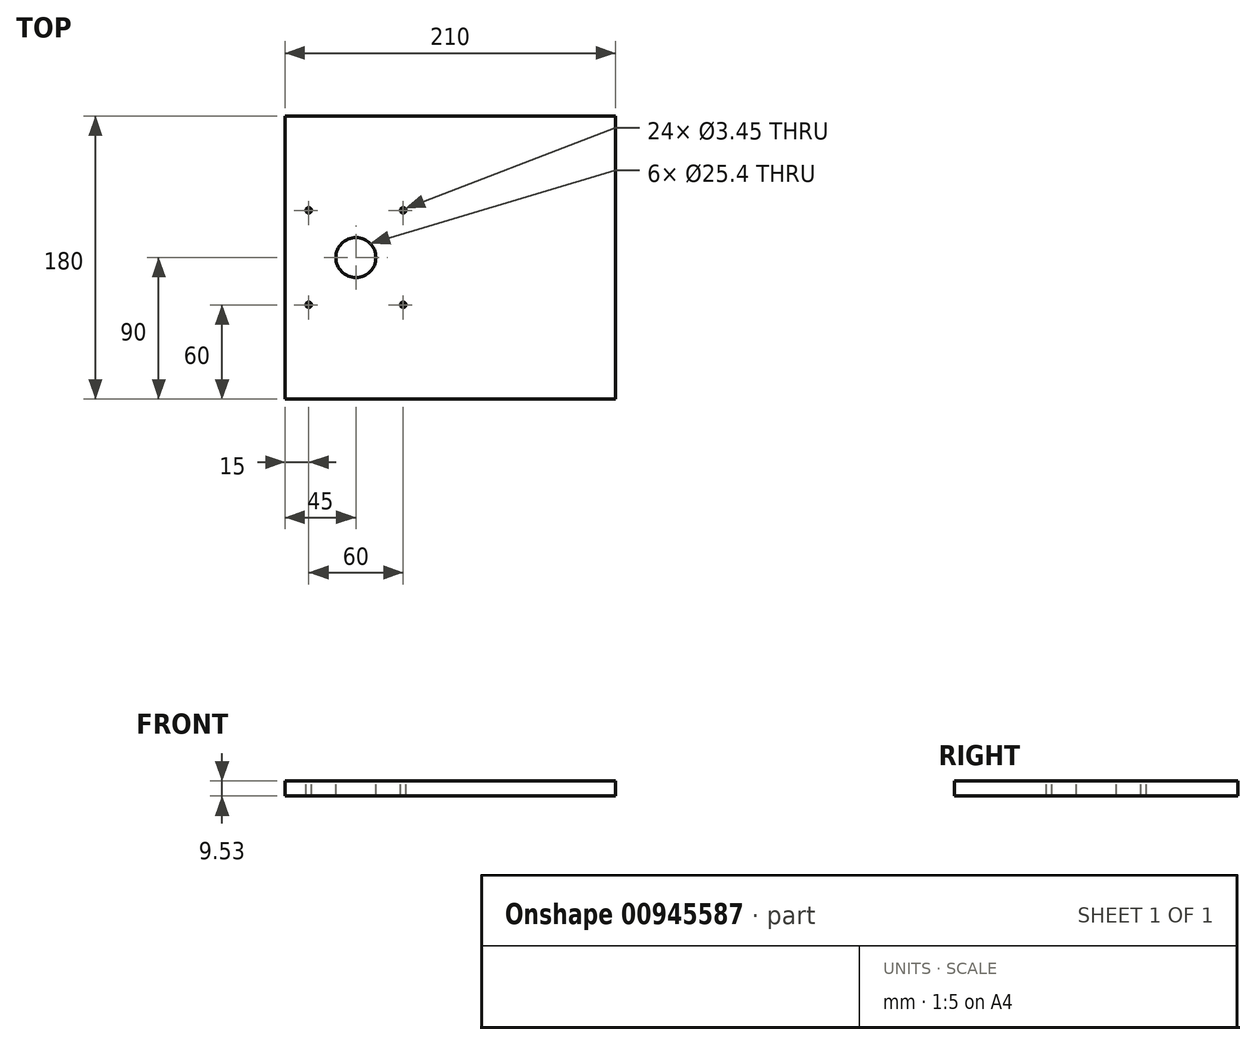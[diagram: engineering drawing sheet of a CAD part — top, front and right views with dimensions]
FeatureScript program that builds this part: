
annotation { "Feature Type Name" : "Feature", "Feature Type Description" : "" }
export const myFeature = defineFeature(function(context is Context, id is Id, definition is map)
    precondition{}
    {
        {
            var Q0;
            Q0=qCreatedBy(makeId("Top.planeOp"),FACE);
            var sketch = newSketch(context, id + "F0", { "sketchPlane" : qUnion([Q0])});
            skLineSegment(sketch, "E0.bottom", {"start": v(105, 90) * mm, "end": v(-105, 90) * mm});
            skLineSegment(sketch, "E0.top", {"start": v(105, -90) * mm, "end": v(-105, -90) * mm});
            skLineSegment(sketch, "E0.left", {"start": v(105, 90) * mm, "end": v(105, -90) * mm});
            skLineSegment(sketch, "E0.right", {"start": v(-105, 90) * mm, "end": v(-105, -90) * mm});
            skPoint(sketch, "E0.middle", {"position": v(0, 0) * mm});
            skSolve(sketch);
        }
        {
            var Q0;
            Q0=qSketchRegion(id+"F0",true);
            extrude(context, id + "F1", {"entities" : qUnion([Q0]), "depth" : 9.52 * mm, "offsetDistance" : 25 * mm});
        }
        {
            var Q0;
            Q0=makeQuery(id+"F1.opExtrude","CAP_FACE",FACE,{"disambiguationData":[OSD([sQuery(id+"F0.wireOp",EDGE,"E0.bottom"),sQuery(id+"F0.wireOp",EDGE,"E0.top"),sQuery(id+"F0.wireOp",EDGE,"E0.left"),sQuery(id+"F0.wireOp",EDGE,"E0.right")])],"isStart":false});
            var sketch = newSketch(context, id + "F2", { "sketchPlane" : qUnion([Q0])});
            skCircle(sketch, "E1", {"center": v(-60, 0) * mm, "radius": 12.7 * mm});
            skCircle(sketch, "E2", {"center": v(-30, 30) * mm, "radius": 1.73 * mm});
            skCircle(sketch, "E3", {"center": v(-30, -30) * mm, "radius": 1.73 * mm});
            skCircle(sketch, "E4", {"center": v(-90, -30) * mm, "radius": 1.73 * mm});
            skCircle(sketch, "E5", {"center": v(-90, 30) * mm, "radius": 1.73 * mm});
            skLineSegment(sketch, "E6", {"start": v(-30, 30) * mm, "end": v(-90, -30) * mm, "construction": true});
            skLineSegment(sketch, "E7", {"start": v(-90, 30) * mm, "end": v(-30, -30) * mm, "construction": true});
            skSolve(sketch);
        }
        {
            var Q0;
            Q0=qSketchRegion(id+"F2",true);
            var Q1;
            Q1=makeQuery(id+"F1.opExtrude","CAP_FACE",FACE,{"disambiguationData":[OSD([sQuery(id+"F0.wireOp",EDGE,"E0.bottom"),sQuery(id+"F0.wireOp",EDGE,"E0.top"),sQuery(id+"F0.wireOp",EDGE,"E0.left"),sQuery(id+"F0.wireOp",EDGE,"E0.right")])],"isStart":true});
            extrude(context, id + "F3", {"entities" : qUnion([Q0]), "operationType" : NewBodyOperationType.REMOVE, "endBound" : BoundingType.UP_TO_SURFACE, "oppositeDirection" : true, "depth" : 25 * mm, "endBoundEntityFace" : qUnion([Q1]), "offsetDistance" : 25 * mm});
        }
    });
